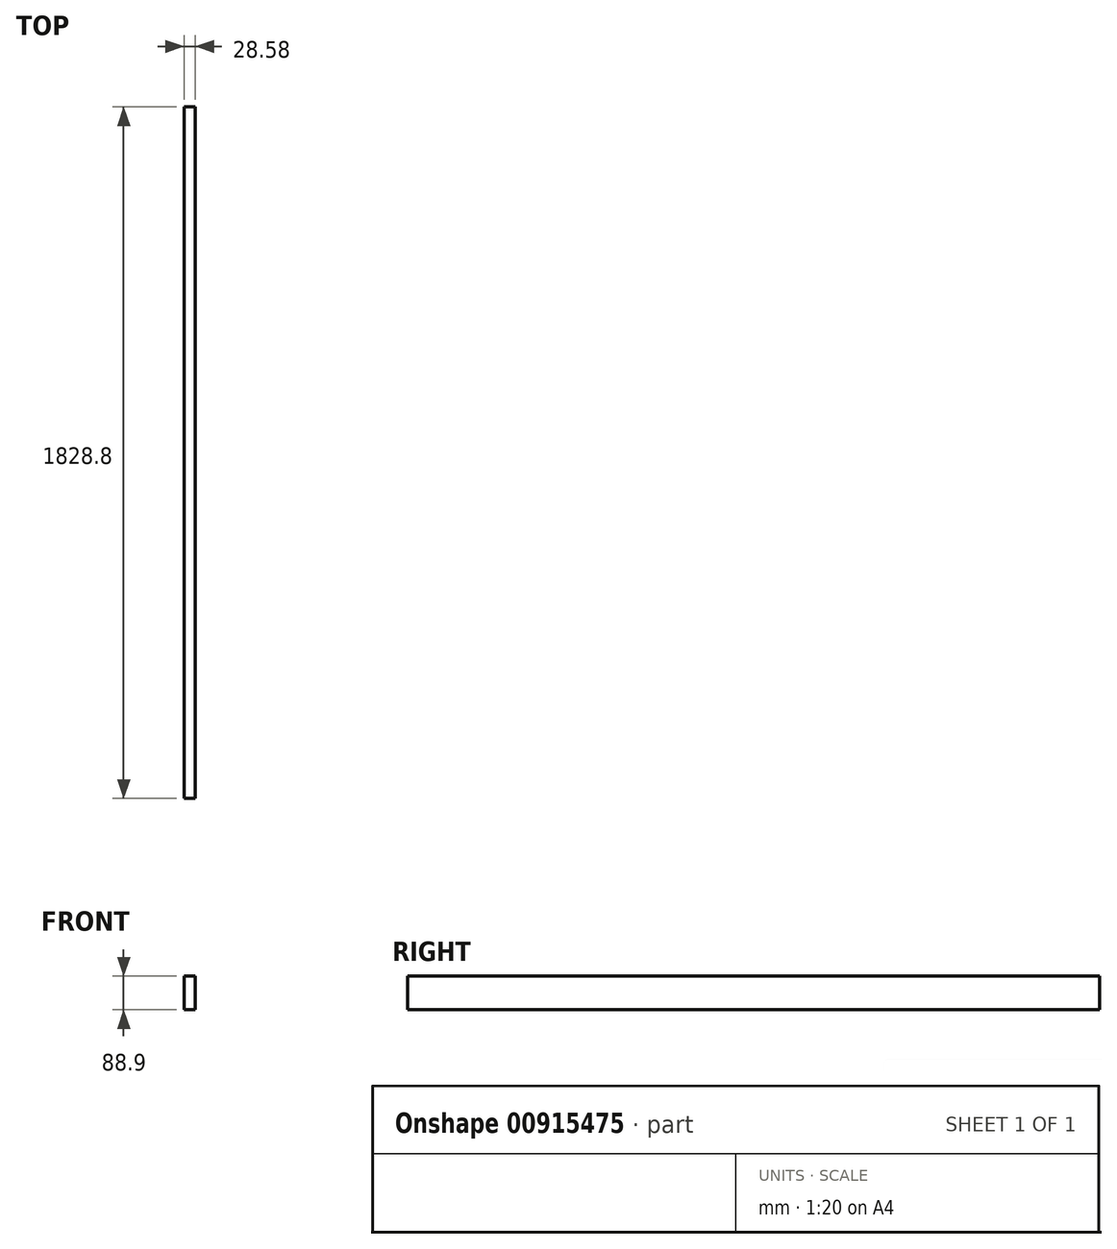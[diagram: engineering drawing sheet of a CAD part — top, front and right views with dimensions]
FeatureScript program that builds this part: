
annotation { "Feature Type Name" : "Feature", "Feature Type Description" : "" }
export const myFeature = defineFeature(function(context is Context, id is Id, definition is map)
    precondition{}
    {
        {
            var Q0;
            Q0=qCreatedBy(makeId("Front.planeOp"),FACE);
            var sketch = newSketch(context, id + "F0", { "sketchPlane" : qUnion([Q0])});
            skLineSegment(sketch, "E0.bottom", {"start": v(-10.57, 53.1) * mm, "end": v(18, 53.1) * mm});
            skLineSegment(sketch, "E0.top", {"start": v(-10.57, -35.8) * mm, "end": v(18, -35.8) * mm});
            skLineSegment(sketch, "E0.left", {"start": v(-10.57, 53.1) * mm, "end": v(-10.57, -35.8) * mm});
            skLineSegment(sketch, "E0.right", {"start": v(18, 53.1) * mm, "end": v(18, -35.8) * mm});
            skSolve(sketch);
        }
        {
            var Q0;
            Q0=makeQuery(id+"F0.imprint","IMPRINT",FACE,{"disambiguationData":[TD([[makeQuery(id+"F0.imprint","IMPRINT",EDGE,{"derivedFrom":sQuery(id+"F0.wireOp",EDGE,"E0.bottom")}),-1.0]])]});
            extrude(context, id + "F1", {"entities" : qUnion([Q0]), "depth" : 1828.8 * mm, "offsetDistance" : 25.4 * mm});
        }
    });
